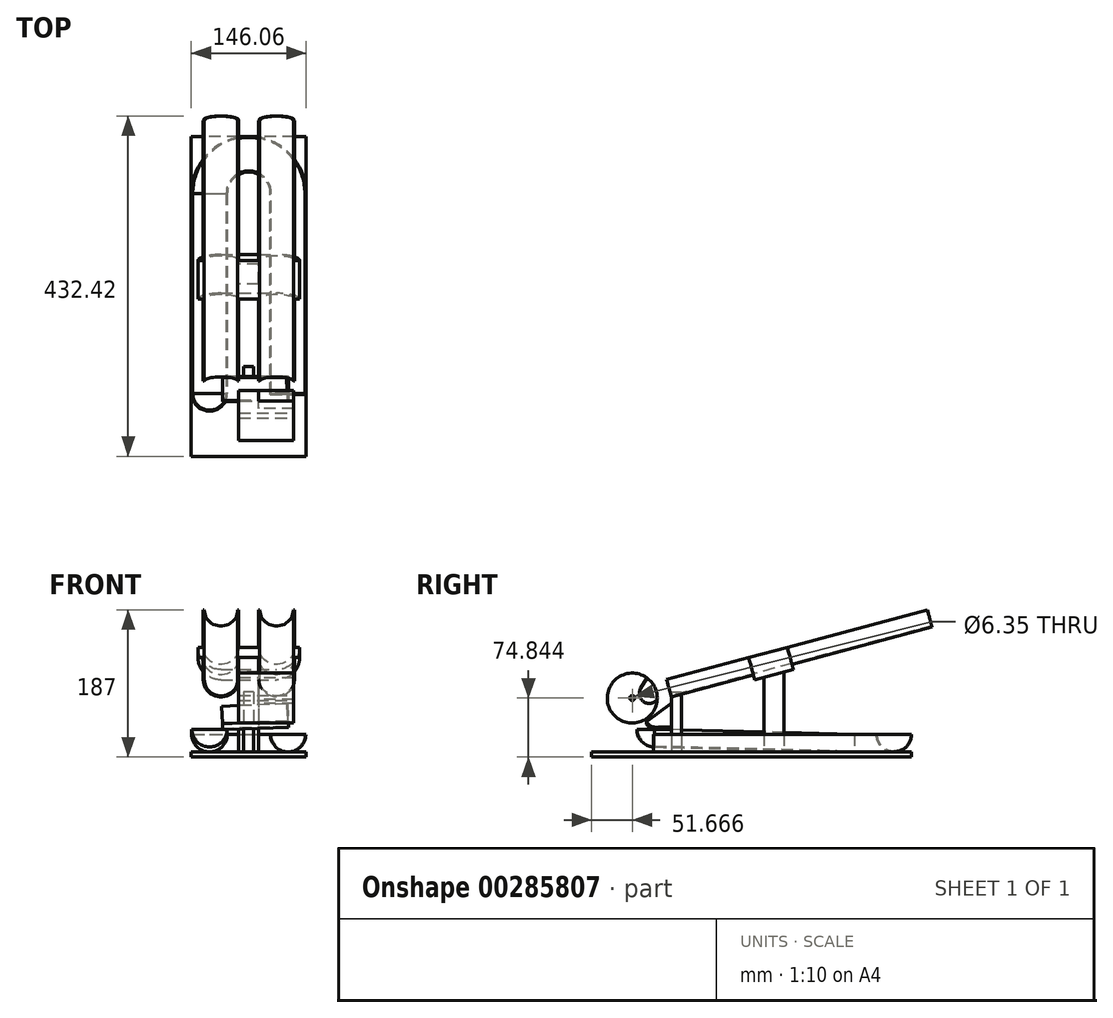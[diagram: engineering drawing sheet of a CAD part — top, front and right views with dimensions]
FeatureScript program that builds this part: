
annotation { "Feature Type Name" : "Feature", "Feature Type Description" : "" }
export const myFeature = defineFeature(function(context is Context, id is Id, definition is map)
    precondition{}
    {
        {
            var Q0;
            Q0=qCreatedBy(makeId("Top.planeOp"),FACE);
            var sketch = newSketch(context, id + "F0", { "sketchPlane" : qUnion([Q0])});
            skArc(sketch, "E0", {"start": v(28.58, 0) * mm, "mid": v(0, 28.58) * mm, "end": v(-28.58, 0) * mm, "construction": true});
            skArc(sketch, "E1.0", {"start": v(71.25, 0) * mm, "mid": v(0, 71.25) * mm, "end": v(-71.25, 0) * mm, "construction": true});
            skArc(sketch, "E2.0", {"start": v(49.91, 0) * mm, "mid": v(0, 49.91) * mm, "end": v(-49.91, 0) * mm});
            skSolve(sketch);
        }
        {
            var Q0;
            Q0=qCreatedBy(makeId("Front.planeOp"),FACE);
            var sketch = newSketch(context, id + "F1", { "sketchPlane" : qUnion([Q0])});
            skArc(sketch, "E3", {"start": v(-28.58, 0) * mm, "mid": v(-49.91, -21.34) * mm, "end": v(-71.25, 0) * mm});
            skArc(sketch, "E4.0", {"start": v(-27.3, 0) * mm, "mid": v(-49.91, -22.6) * mm, "end": v(-72.52, 0) * mm});
            skLineSegment(sketch, "E5", {"start": v(-72.52, 0) * mm, "end": v(-71.25, 0) * mm});
            skLineSegment(sketch, "E6", {"start": v(-28.58, 0) * mm, "end": v(-27.3, 0) * mm});
            skLineSegment(sketch, "E7", {"start": v(-49.91, 0) * mm, "end": v(-49.91, 31.81) * mm, "construction": true});
            skSolve(sketch);
        }
        {
            var Q0;
            Q0 = qSketchRegion(id + "F1", true);
            var Q1;
            Q1=sQuery(id+"F0.wireOp",EDGE,"E2.0");
            sweep(context, id + "F2", {"profiles" : qUnion([Q0]), "path" : qUnion([Q1])});
        }
        {
            var Q0;
            Q0=qCreatedBy(makeId("Right.planeOp"),FACE);
            cPlane(context, id + "F3", {"entities" : qUnion([Q0]), "cplaneType" : CPlaneType.OFFSET, "offset" : 49.9 * mm, "oppositeDirection" : true, "width" : 152.4 * mm, "height" : 152.4 * mm});
        }
        {
            var Q0;
            Q0=makeQuery(id+"F2.opSweep","CAP_FACE",FACE,{"disambiguationData":[OSD([sQuery(id+"F0.wireOp",VERTEX,"E2.0.start"),sQuery(id+"F1.wireOp",EDGE,"E3"),sQuery(id+"F1.wireOp",EDGE,"E4.0"),sQuery(id+"F1.wireOp",EDGE,"E5"),sQuery(id+"F1.wireOp",EDGE,"E6")])],"isStart":false});
            extrude(context, id + "F4", {"entities" : qUnion([Q0]), "operationType" : NewBodyOperationType.ADD, "depth" : 254 * mm});
        }
        {
            var Q0;
            Q0=qCreatedBy(id+"F3.planeOp",FACE);
            var sketch = newSketch(context, id + "F5", { "sketchPlane" : qUnion([Q0])});
            skLineSegment(sketch, "E8", {"start": v(0, 0) * mm, "end": v(-253.92, 6.35) * mm});
            skSolve(sketch);
        }
        {
            var Q0;
            Q0 = qSketchRegion(id + "F1", true);
            var Q1;
            Q1 = qConstructionFilter(qBodyType(qCreatedBy(id + "F5" ,EDGE), BodyType.WIRE), ConstructionObject.NO);
            sweep(context, id + "F6", {"operationType" : NewBodyOperationType.ADD, "profiles" : qUnion([Q0]), "path" : qUnion([Q1])});
        }
        {
            var Q0;
            Q0=makeQuery(id+"F4.opExtrude","CAP_FACE",FACE,{"disambiguationData":[OSD([sQuery(id+"F0.wireOp",VERTEX,"E2.0.start"),sQuery(id+"F1.wireOp",EDGE,"E3"),sQuery(id+"F1.wireOp",EDGE,"E4.0"),sQuery(id+"F1.wireOp",EDGE,"E5"),sQuery(id+"F1.wireOp",EDGE,"E6")])],"isStart":false});
            var sketch = newSketch(context, id + "F7", { "sketchPlane" : qUnion([Q0])});
            skLineSegment(sketch, "E9", {"start": v(27.3, 0) * mm, "end": v(72.52, 0) * mm});
            skArc(sketch, "E10", {"start": v(27.3, 0) * mm, "mid": v(49.91, -22.6) * mm, "end": v(72.52, 0) * mm});
            skLineSegment(sketch, "E11", {"start": v(27.3, 0) * mm, "end": v(28.57, 0) * mm});
            skSolve(sketch);
        }
        {
            var Q0;
            Q0 = qSketchRegion(id + "F7", true);
            extrude(context, id + "F8", {"entities" : qUnion([Q0]), "operationType" : NewBodyOperationType.ADD, "depth" : 1.27 * mm});
        }
        {
            var Q0;
            Q0=makeQuery(id+"F6.opSweep","CAP_FACE",FACE,{"disambiguationData":[OSD([sQuery(id+"F1.wireOp",EDGE,"E3"),sQuery(id+"F1.wireOp",EDGE,"E4.0"),sQuery(id+"F1.wireOp",EDGE,"E5"),sQuery(id+"F1.wireOp",EDGE,"E6"),sQuery(id+"F5.wireOp",VERTEX,"E8.end")])],"isStart":false});
            var sketch = newSketch(context, id + "F9", { "sketchPlane" : qUnion([Q0])});
            skLineSegment(sketch, "E12", {"start": v(-49.91, 6.35) * mm, "end": v(-49.91, -35.67) * mm, "construction": true});
            skLineSegment(sketch, "E13", {"start": v(-71.25, 6.35) * mm, "end": v(-72.52, 6.35) * mm});
            skArc(sketch, "E14", {"start": v(-71.25, 6.35) * mm, "mid": v(-65, -8.74) * mm, "end": v(-49.91, -14.99) * mm});
            skArc(sketch, "E15.0", {"start": v(-72.52, 6.35) * mm, "mid": v(-65.9, -9.63) * mm, "end": v(-49.91, -16.26) * mm});
            skLineSegment(sketch, "E16", {"start": v(-49.91, -14.99) * mm, "end": v(-49.91, -16.26) * mm});
            skSolve(sketch);
        }
        {
            var Q0;
            Q0 = qSketchRegion(id + "F9", true);
            var Q1;
            Q1=sQuery(id+"F9.wireOp",EDGE,"E12");
            revolve(context, id + "F10", {"operationType" : NewBodyOperationType.ADD, "entities" : qUnion([Q0]), "axis" : qUnion([Q1]), "revolveType" : RevolveType.ONE_DIRECTION, "oppositeDirection" : true, "angle" : 180 * degree});
        }
        {
            var Q0;
            Q0=qCreatedBy(makeId("Top.planeOp"),FACE);
            cPlane(context, id + "F11", {"entities" : qUnion([Q0]), "cplaneType" : CPlaneType.OFFSET, "offset" : 22.6 * mm, "oppositeDirection" : true, "width" : 152.4 * mm, "height" : 152.4 * mm});
        }
        {
            var Q0;
            Q0=qCreatedBy(id+"F11.planeOp",FACE);
            var sketch = newSketch(context, id + "F12", { "sketchPlane" : qUnion([Q0])});
            skLineSegment(sketch, "E17.bottom", {"start": v(73.03, 72.52) * mm, "end": v(-73.03, 72.52) * mm});
            skLineSegment(sketch, "E17.top", {"start": v(73.03, -333.88) * mm, "end": v(-73.03, -333.88) * mm});
            skLineSegment(sketch, "E17.left", {"start": v(73.03, 72.52) * mm, "end": v(73.03, -333.88) * mm});
            skLineSegment(sketch, "E17.right", {"start": v(-73.03, 72.52) * mm, "end": v(-73.03, -333.88) * mm});
            skSolve(sketch);
        }
        {
            var Q0;
            Q0 = qSketchRegion(id + "F12", true);
            extrude(context, id + "F13", {"entities" : qUnion([Q0]), "operationType" : NewBodyOperationType.ADD, "oppositeDirection" : true, "depth" : 6.35 * mm});
        }
        {
            var Q0;
            Q0=makeQuery(id+"F13.opExtrude","CAP_FACE",FACE,{"disambiguationData":[OSD([sQuery(id+"F12.wireOp",EDGE,"E17.bottom"),sQuery(id+"F12.wireOp",EDGE,"E17.top"),sQuery(id+"F12.wireOp",EDGE,"E17.left"),sQuery(id+"F12.wireOp",EDGE,"E17.right")])],"isStart":true});
            var sketch = newSketch(context, id + "F14", { "sketchPlane" : qUnion([Q0])});
            skLineSegment(sketch, "E18", {"start": v(0, 5.8) * mm, "end": v(0, -333.88) * mm, "construction": true});
            skLineSegment(sketch, "E19", {"start": v(-73.03, -102.16) * mm, "end": v(73.03, -102.16) * mm, "construction": true});
            skLineSegment(sketch, "E20.bottom", {"start": v(12.7, -114.86) * mm, "end": v(-12.7, -114.86) * mm});
            skLineSegment(sketch, "E20.top", {"start": v(12.7, -89.46) * mm, "end": v(-12.7, -89.46) * mm});
            skLineSegment(sketch, "E20.left", {"start": v(12.7, -114.86) * mm, "end": v(12.7, -89.46) * mm});
            skLineSegment(sketch, "E20.right", {"start": v(-12.7, -114.86) * mm, "end": v(-12.7, -89.46) * mm});
            skPoint(sketch, "E20.middle", {"position": v(0, -102.16) * mm});
            skSolve(sketch);
        }
        {
            var Q0;
            Q0=makeQuery(id+"F14.imprint","IMPRINT",FACE,{"disambiguationData":[TD([[makeQuery(id+"F14.imprint","IMPRINT",EDGE,{"derivedFrom":sQuery(id+"F14.wireOp",EDGE,"E20.bottom")}),-1.0]])]});
            extrude(context, id + "F15", {"entities" : qUnion([Q0]), "operationType" : NewBodyOperationType.ADD, "depth" : 101.6 * mm});
        }
        {
            var Q0;
            Q0=makeQuery(id+"F15.opExtrude","SWEPT_FACE",FACE,{"disambiguationData":[OSD([sQuery(id+"F14.wireOp",EDGE,"E20.left")])]});
            var sketch = newSketch(context, id + "F16", { "sketchPlane" : qUnion([Q0])});
            skLineSegment(sketch, "E21", {"start": v(-89.46, 79) * mm, "end": v(-114.86, 72.19) * mm});
            skLineSegment(sketch, "E22", {"start": v(-114.86, 72.19) * mm, "end": v(-114.86, 79) * mm});
            skLineSegment(sketch, "E23", {"start": v(-114.86, 79) * mm, "end": v(-89.46, 79) * mm});
            skSolve(sketch);
        }
        {
            var Q0;
            Q0=makeQuery(id+"F16.imprint","IMPRINT",FACE,{"disambiguationData":[TD([[makeQuery(id+"F16.imprint","IMPRINT",EDGE,{"derivedFrom":sQuery(id+"F16.wireOp",EDGE,"E21")}),-1.0]])]});
            extrude(context, id + "F17", {"entities" : qUnion([Q0]), "operationType" : NewBodyOperationType.REMOVE, "endBound" : BoundingType.THROUGH_ALL, "oppositeDirection" : true, "depth" : 25.4 * mm});
        }
        {
            var Q0;
            Q0=makeQuery(id+"F17.boolean.opBoolean","COPY",FACE,{"derivedFrom":makeQuery(id+"F17.opExtrude","SWEPT_FACE",FACE,{"disambiguationData":[OSD([sQuery(id+"F16.wireOp",EDGE,"E21")])]})});
            var sketch = newSketch(context, id + "F18", { "sketchPlane" : qUnion([Q0])});
            skLineSegment(sketch, "E24", {"start": v(-12.7, -79.11) * mm, "end": v(12.7, -79.11) * mm, "construction": true});
            skSolve(sketch);
        }
        {
            var Q0;
            Q0=sQuery(id+"F18.wireOp",EDGE,"E24");
            cPlane(context, id + "F19", {"entities" : qUnion([Q0]), "cplaneType" : CPlaneType.LINE_ANGLE, "offset" : 25.4 * mm, "angle" : 15 * degree, "width" : 152.4 * mm, "height" : 152.4 * mm});
        }
        {
            var Q0;
            Q0=qCreatedBy(id+"F19.planeOp",FACE);
            var sketch = newSketch(context, id + "F20", { "sketchPlane" : qUnion([Q0])});
            skLineSegment(sketch, "E25", {"start": v(0, 75.34) * mm, "end": v(0, 143.85) * mm, "construction": true});
            skLineSegment(sketch, "E26", {"start": v(-12.7, 128.67) * mm, "end": v(12.7, 128.67) * mm});
            skCircle(sketch, "E27", {"center": v(-35.3, 128.67) * mm, "radius": 22.6 * mm, "construction": true});
            skCircle(sketch, "E28.MirrorC", {"center": v(35.3, 128.67) * mm, "radius": 22.6 * mm, "construction": true});
            skLineSegment(sketch, "E29", {"start": v(-12.7, 99.46) * mm, "end": v(12.7, 99.46) * mm});
            skLineSegment(sketch, "E30", {"start": v(-12.7, 99.46) * mm, "end": v(-35.3, 99.46) * mm});
            skLineSegment(sketch, "E31", {"start": v(12.7, 99.46) * mm, "end": v(35.3, 99.46) * mm});
            skArc(sketch, "E32", {"start": v(-35.3, 99.46) * mm, "mid": v(-55.96, 108.01) * mm, "end": v(-64.52, 128.67) * mm});
            skArc(sketch, "E33", {"start": v(35.3, 99.46) * mm, "mid": v(55.96, 108.01) * mm, "end": v(64.52, 128.67) * mm});
            skLineSegment(sketch, "E34", {"start": v(-64.52, 128.67) * mm, "end": v(-57.91, 128.67) * mm});
            skLineSegment(sketch, "E35", {"start": v(64.52, 128.67) * mm, "end": v(57.91, 128.67) * mm});
            skArc(sketch, "E36", {"start": v(-57.91, 128.67) * mm, "mid": v(-35.3, 106.06) * mm, "end": v(-12.7, 128.67) * mm});
            skArc(sketch, "E37", {"start": v(12.7, 128.67) * mm, "mid": v(35.3, 106.06) * mm, "end": v(57.91, 128.67) * mm});
            skSolve(sketch);
        }
        {
            var Q0;
            Q0=makeQuery(id+"F20.imprint","IMPRINT",FACE,{"disambiguationData":[TD([[makeQuery(id+"F20.imprint","IMPRINT",EDGE,{"derivedFrom":sQuery(id+"F20.wireOp",EDGE,"E26")}),-1.0]])]});
            extrude(context, id + "F21", {"entities" : qUnion([Q0]), "operationType" : NewBodyOperationType.ADD, "endBound" : BoundingType.SYMMETRIC, "depth" : 50.8 * mm});
        }
        {
            var Q0;
            Q0=qCreatedBy(id+"F11.planeOp",FACE);
            var sketch = newSketch(context, id + "F22", { "sketchPlane" : qUnion([Q0])});
            skLineSegment(sketch, "E38.0", {"start": v(28.58, -254) * mm, "end": v(71.25, -254) * mm});
            skLineSegment(sketch, "E39", {"start": v(28.58, -254) * mm, "end": v(-89.3, -254) * mm, "construction": true});
            skLineSegment(sketch, "E40", {"start": v(0, -226.31) * mm, "end": v(0, -343.32) * mm, "construction": true});
            skLineSegment(sketch, "E41.bottom", {"start": v(6.35, -232.66) * mm, "end": v(-6.35, -232.66) * mm});
            skLineSegment(sketch, "E41.top", {"start": v(6.35, -219.96) * mm, "end": v(-6.35, -219.96) * mm});
            skLineSegment(sketch, "E41.left", {"start": v(6.35, -232.66) * mm, "end": v(6.35, -219.96) * mm});
            skLineSegment(sketch, "E41.right", {"start": v(-6.35, -232.66) * mm, "end": v(-6.35, -219.96) * mm});
            skPoint(sketch, "E41.middle", {"position": v(0, -226.31) * mm});
            skSolve(sketch);
        }
        {
            var Q0;
            Q0=qCreatedBy(id+"F19.planeOp",FACE);
            cPlane(context, id + "F23", {"entities" : qUnion([Q0]), "cplaneType" : CPlaneType.OFFSET, "offset" : 38.1 * mm, "width" : 152.4 * mm, "height" : 152.4 * mm});
        }
        {
            var Q0;
            Q0=qCreatedBy(id+"F23.planeOp",FACE);
            var sketch = newSketch(context, id + "F24", { "sketchPlane" : qUnion([Q0])});
            skArc(sketch, "E42.0.0", {"start": v(57.91, 128.67) * mm, "mid": v(35.3, 106.06) * mm, "end": v(12.7, 128.67) * mm});
            skArc(sketch, "E42.0.2", {"start": v(12.7, 128.67) * mm, "mid": v(35.3, 106.06) * mm, "end": v(57.91, 128.67) * mm});
            skArc(sketch, "E43.0.0", {"start": v(-12.7, 128.67) * mm, "mid": v(-35.3, 106.06) * mm, "end": v(-57.91, 128.67) * mm});
            skArc(sketch, "E43.0.2", {"start": v(-57.91, 128.67) * mm, "mid": v(-35.3, 106.06) * mm, "end": v(-12.7, 128.67) * mm});
            skArc(sketch, "E44.0", {"start": v(-56.64, 128.67) * mm, "mid": v(-35.3, 107.33) * mm, "end": v(-13.97, 128.67) * mm});
            skArc(sketch, "E45.0", {"start": v(13.97, 128.67) * mm, "mid": v(35.3, 107.33) * mm, "end": v(56.64, 128.67) * mm});
            skLineSegment(sketch, "E46", {"start": v(-12.7, 128.67) * mm, "end": v(-13.97, 128.67) * mm});
            skLineSegment(sketch, "E47", {"start": v(-56.64, 128.67) * mm, "end": v(-57.91, 128.67) * mm});
            skLineSegment(sketch, "E48", {"start": v(12.7, 128.67) * mm, "end": v(13.97, 128.67) * mm});
            skLineSegment(sketch, "E49", {"start": v(56.64, 128.67) * mm, "end": v(57.91, 128.67) * mm});
            skSolve(sketch);
        }
        {
            var Q0;
            Q0 = qSketchRegion(id + "F24", true);
            extrude(context, id + "F25", {"entities" : qUnion([Q0]), "operationType" : NewBodyOperationType.ADD, "endBound" : BoundingType.SYMMETRIC, "depth" : 342.9 * mm});
        }
        {
            var Q0;
            Q0=makeQuery(id+"F22.imprint","IMPRINT",FACE,{"disambiguationData":[TD([[makeQuery(id+"F22.imprint","IMPRINT",EDGE,{"derivedFrom":sQuery(id+"F22.wireOp",EDGE,"E41.bottom")}),-1.0]])]});
            extrude(context, id + "F26", {"entities" : qUnion([Q0]), "operationType" : NewBodyOperationType.ADD, "depth" : 76.2 * mm});
        }
        {
            var Q0;
            Q0=makeQuery(id+"F26.opExtrude","CAP_EDGE",EDGE,{"disambiguationData":[OSD([sQuery(id+"F22.wireOp",EDGE,"E41.left")])],"isStart":false});
            cPlane(context, id + "F27", {"entities" : qUnion([Q0]), "cplaneType" : CPlaneType.LINE_ANGLE, "offset" : 25.4 * mm, "angle" : 88 * degree, "width" : 152.4 * mm, "height" : 152.4 * mm});
        }
        {
            var Q0;
            Q0=qCreatedBy(id+"F27.planeOp",FACE);
            var sketch = newSketch(context, id + "F28", { "sketchPlane" : qUnion([Q0])});
            skLineSegment(sketch, "E50.0.0", {"start": v(-232.66, -22.37) * mm, "end": v(-232.66, -22.81) * mm});
            skLineSegment(sketch, "E50.0.1", {"start": v(-232.66, -22.81) * mm, "end": v(-232.66, 53.34) * mm});
            skLineSegment(sketch, "E50.0.2", {"start": v(-232.66, 53.34) * mm, "end": v(-232.66, 53.78) * mm});
            skLineSegment(sketch, "E50.0.3", {"start": v(-232.66, 53.78) * mm, "end": v(-232.66, -22.37) * mm});
            skLineSegment(sketch, "E51.0", {"start": v(0, 0.95) * mm, "end": v(-253.92, 7.3) * mm});
            skLineSegment(sketch, "E52", {"start": v(-232.66, 36.69) * mm, "end": v(-232.66, 6.77) * mm});
            skLineSegment(sketch, "E53", {"start": v(-232.66, 6.77) * mm, "end": v(-253.92, 7.3) * mm});
            skArc(sketch, "E54", {"start": v(-253.92, 7.3) * mm, "mid": v(-260.15, 9.32) * mm, "end": v(-264.27, 14.42) * mm});
            skArc(sketch, "E55.0", {"start": v(-253.89, 8.57) * mm, "mid": v(-259.43, 10.37) * mm, "end": v(-263.09, 14.9) * mm});
            skLineSegment(sketch, "E55.1", {"start": v(-233.93, 8.07) * mm, "end": v(-253.89, 8.57) * mm});
            skLineSegment(sketch, "E55.2", {"start": v(-233.93, 36.69) * mm, "end": v(-233.93, 8.07) * mm});
            skLineSegment(sketch, "E56", {"start": v(-232.66, 36.69) * mm, "end": v(-233.93, 36.69) * mm});
            skLineSegment(sketch, "E57", {"start": v(-263.09, 14.9) * mm, "end": v(-264.27, 14.42) * mm});
            skSolve(sketch);
        }
        {
            var Q0;
            Q0 = qSketchRegion(id + "F28", true);
            extrude(context, id + "F29", {"entities" : qUnion([Q0]), "endBound" : BoundingType.SYMMETRIC, "depth" : 82.55 * mm});
        }
        {
            var Q0;
            Q0=makeQuery(id+"F29.opExtrude","CAP_FACE",FACE,{"disambiguationData":[OSD([sQuery(id+"F28.wireOp",EDGE,"E52"),sQuery(id+"F28.wireOp",EDGE,"E53"),sQuery(id+"F28.wireOp",EDGE,"E54"),sQuery(id+"F28.wireOp",EDGE,"E55.0"),sQuery(id+"F28.wireOp",EDGE,"E55.1"),sQuery(id+"F28.wireOp",EDGE,"E55.2"),sQuery(id+"F28.wireOp",EDGE,"E56"),sQuery(id+"F28.wireOp",EDGE,"E57")])],"isStart":false});
            var sketch = newSketch(context, id + "F30", { "sketchPlane" : qUnion([Q0])});
            skLineSegment(sketch, "E58", {"start": v(-233.93, 36.69) * mm, "end": v(-263.09, 14.9) * mm});
            skLineSegment(sketch, "E59", {"start": v(-263.09, 14.9) * mm, "end": v(-264.27, 14.42) * mm});
            skArc(sketch, "E60.0", {"start": v(-253.92, 7.3) * mm, "mid": v(-260.15, 9.32) * mm, "end": v(-264.27, 14.42) * mm});
            skLineSegment(sketch, "E60.1", {"start": v(-232.66, 6.77) * mm, "end": v(-253.92, 7.3) * mm});
            skLineSegment(sketch, "E60.2", {"start": v(-232.66, 36.69) * mm, "end": v(-232.66, 6.77) * mm});
            skSolve(sketch);
        }
        {
            var Q0;
            Q0=makeQuery(id+"F30.imprint","IMPRINT",FACE,{"disambiguationData":[TD([[makeQuery(id+"F30.imprint","IMPRINT",EDGE,{"derivedFrom":sQuery(id+"F30.wireOp",EDGE,"E59")}),1.0]])]});
            var Q1;
            Q1=makeQuery(id+"F30.imprint","IMPRINT",FACE,{"disambiguationData":[TD([[makeQuery(id+"F30.imprint","IMPRINT",EDGE,{"derivedFrom":sQuery(id+"F30.wireOp",EDGE,"E58")}),1.0]])]});
            extrude(context, id + "F31", {"entities" : qUnion([Q0, Q1]), "operationType" : NewBodyOperationType.ADD, "depth" : 1.27 * mm});
        }
        {
            var Q0;
            Q0=qCreatedBy(makeId("Right.planeOp"),FACE);
            var sketch = newSketch(context, id + "F32", { "sketchPlane" : qUnion([Q0])});
            skLineSegment(sketch, "E61.0", {"start": v(-233.93, 9.8) * mm, "end": v(-233.93, 6.91) * mm});
            skLineSegment(sketch, "E62.0", {"start": v(92.7, 158.04) * mm, "end": v(-238.52, 69.3) * mm});
            skLineSegment(sketch, "E63.0", {"start": v(-238.52, 69.3) * mm, "end": v(-232.67, 47.46) * mm});
            skPoint(sketch, "E64", {"position": v(-235.6, 58.37) * mm});
            skLineSegment(sketch, "E65", {"start": v(-235.6, 58.37) * mm, "end": v(-328.83, 33.4) * mm, "construction": true});
            skCircle(sketch, "E66", {"center": v(-282.21, 45.88) * mm, "radius": 31.75 * mm});
            skSolve(sketch);
        }
        {
            var Q0;
            Q0=makeQuery(id+"F32.imprint","IMPRINT",FACE,{"disambiguationData":[TD([[makeQuery(id+"F32.imprint","IMPRINT",EDGE,{"derivedFrom":sQuery(id+"F32.wireOp",EDGE,"E66")}),1.0]])]});
            extrude(context, id + "F33", {"entities" : qUnion([Q0]), "endBound" : BoundingType.SYMMETRIC, "depth" : 25.4 * mm});
        }
        {
            var Q0;
            Q0=makeQuery(id+"F33.opExtrude","CAP_FACE",FACE,{"disambiguationData":[OSD([sQuery(id+"F32.wireOp",EDGE,"E66")])],"isStart":false});
            var sketch = newSketch(context, id + "F34", { "sketchPlane" : qUnion([Q0])});
            skArc(sketch, "E67.0", {"start": v(-263.82, 71.76) * mm, "mid": v(-310.85, 32.17) * mm, "end": v(-250.52, 43.99) * mm});
            skLineSegment(sketch, "E68", {"start": v(-282.21, 45.88) * mm, "end": v(-200.7, 67.72) * mm, "construction": true});
            skLineSegment(sketch, "E69.0", {"start": v(-238.52, 69.3) * mm, "end": v(-233, 48.68) * mm});
            skLineSegment(sketch, "E70", {"start": v(-233, 48.68) * mm, "end": v(-280.04, 36.08) * mm, "construction": true});
            skPoint(sketch, "E71", {"position": v(-250.52, 43.99) * mm});
            skArc(sketch, "E72", {"start": v(-271.64, 57.99) * mm, "mid": v(-267.62, 41.13) * mm, "end": v(-250.52, 43.99) * mm});
            skLineSegment(sketch, "E73", {"start": v(-271.64, 57.99) * mm, "end": v(-263.82, 71.76) * mm});
            skSolve(sketch);
        }
        {
            var Q0;
            Q0=makeQuery(id+"F34.imprint","IMPRINT",FACE,{"disambiguationData":[TD([[makeQuery(id+"F34.imprint","IMPRINT",EDGE,{"derivedFrom":sQuery(id+"F34.wireOp",EDGE,"E67.0")}),1.0]])]});
            extrude(context, id + "F35", {"entities" : qUnion([Q0]), "operationType" : NewBodyOperationType.ADD, "depth" : 43.18 * mm});
        }
        {
            var Q0;
            Q0=makeQuery(id+"F35.opExtrude","CAP_FACE",FACE,{"disambiguationData":[OSD([sQuery(id+"F34.wireOp",EDGE,"E67.0"),sQuery(id+"F34.wireOp",EDGE,"E72"),sQuery(id+"F34.wireOp",EDGE,"E73")])],"isStart":false});
            var sketch = newSketch(context, id + "F36", { "sketchPlane" : qUnion([Q0])});
            skArc(sketch, "E74.0", {"start": v(-263.82, 71.76) * mm, "mid": v(-310.85, 32.17) * mm, "end": v(-250.52, 43.99) * mm});
            skArc(sketch, "E75", {"start": v(-263.82, 71.76) * mm, "mid": v(-253.58, 59.6) * mm, "end": v(-250.52, 43.99) * mm});
            skSolve(sketch);
        }
        {
            var Q0;
            Q0=makeQuery(id+"F36.imprint","IMPRINT",FACE,{"disambiguationData":[TD([[makeQuery(id+"F36.imprint","IMPRINT",EDGE,{"derivedFrom":sQuery(id+"F36.wireOp",EDGE,"E75")}),-1.0]])]});
            var Q1;
            Q1=makeQuery(id+"F36.imprint","IMPRINT",FACE,{"disambiguationData":[TD([[makeQuery(id+"F36.imprint","IMPRINT",EDGE,{"derivedFrom":sQuery(id+"F36.wireOp",EDGE,"E74.0")}),1.0]])]});
            extrude(context, id + "F37", {"entities" : qUnion([Q0, Q1]), "operationType" : NewBodyOperationType.ADD, "depth" : 1.27 * mm});
        }
        {
            var Q0;
            Q0=makeQuery(id+"F37.opExtrude","CAP_FACE",FACE,{"disambiguationData":[OSD([sQuery(id+"F36.wireOp",EDGE,"E74.0"),sQuery(id+"F36.wireOp",EDGE,"E75")])],"isStart":false});
            var sketch = newSketch(context, id + "F38", { "sketchPlane" : qUnion([Q0])});
            skCircle(sketch, "E76.0", {"center": v(-282.21, 45.88) * mm, "radius": 31.75 * mm});
            skCircle(sketch, "E77", {"center": v(-282.21, 45.88) * mm, "radius": 3.18 * mm});
            skSolve(sketch);
        }
        {
            var Q0;
            Q0=makeQuery(id+"F38.imprint","IMPRINT",FACE,{"disambiguationData":[TD([[makeQuery(id+"F38.imprint","IMPRINT",EDGE,{"derivedFrom":sQuery(id+"F38.wireOp",EDGE,"E77")}),1.0]])]});
            var Q1;
            Q1=sQuery(id+"F38.wireOp",EDGE,"E77");
            extrude(context, id + "F39", {"entities" : qUnion([Q0]), "operationType" : NewBodyOperationType.REMOVE, "surfaceEntities" : qUnion([Q1]), "endBound" : BoundingType.THROUGH_ALL, "oppositeDirection" : true, "depth" : 25.4 * mm});
        }
    });
